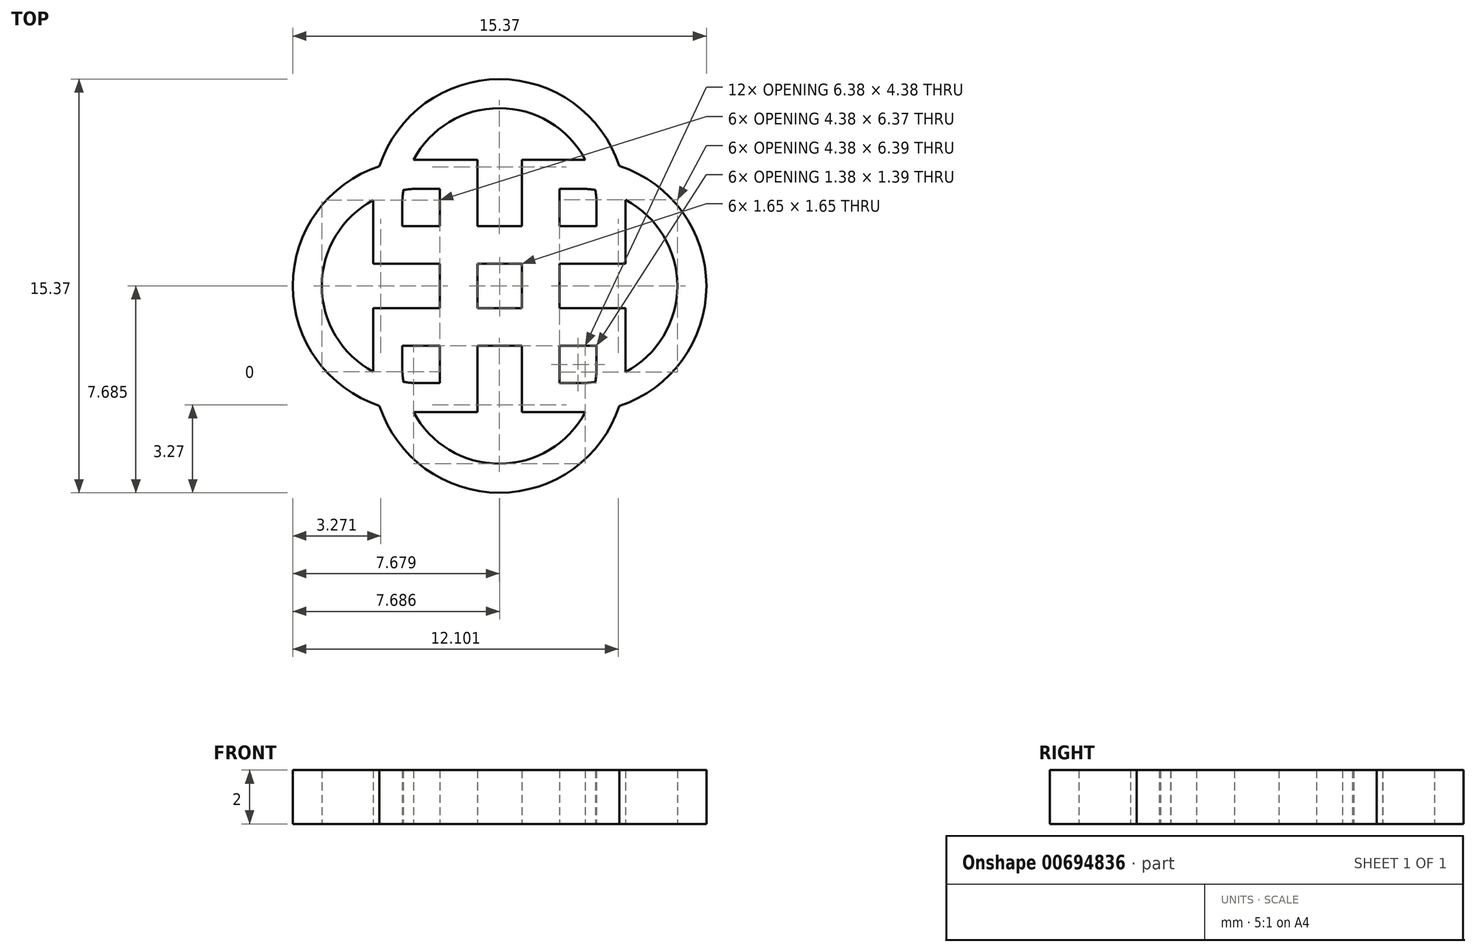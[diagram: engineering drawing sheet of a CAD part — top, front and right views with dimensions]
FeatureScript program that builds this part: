
annotation { "Feature Type Name" : "Feature", "Feature Type Description" : "" }
export const myFeature = defineFeature(function(context is Context, id is Id, definition is map)
    precondition{}
    {
        {
            var Q0;
            Q0=qCreatedBy(makeId("Top.planeOp"),FACE);
            var sketch = newSketch(context, id + "F0", { "sketchPlane" : qUnion([Q0])});
            skPoint(sketch, "E0", {"position": v(-20.72, -15.85) * mm});
            skPoint(sketch, "E1", {"position": v(-17.72, -15.85) * mm});
            skArc(sketch, "E2", {"start": v(-20.72, -11.16) * mm, "mid": v(-25.4, -15.85) * mm, "end": v(-20.72, -20.53) * mm});
            skArc(sketch, "E3", {"start": v(-20.72, -12.24) * mm, "mid": v(-24.33, -15.85) * mm, "end": v(-20.72, -19.46) * mm});
            skLineSegment(sketch, "E4", {"start": v(-20.72, -10.41) * mm, "end": v(-20.72, -21) * mm, "construction": true});
            skLineSegment(sketch, "E5", {"start": v(-20.72, -11.16) * mm, "end": v(-18.55, -11.16) * mm});
            skLineSegment(sketch, "E6", {"start": v(-18.55, -11.16) * mm, "end": v(-18.55, -20.53) * mm});
            skLineSegment(sketch, "E7", {"start": v(-18.55, -20.53) * mm, "end": v(-20.72, -20.53) * mm});
            skLineSegment(sketch, "E8", {"start": v(-20.72, -12.24) * mm, "end": v(-19.95, -12.24) * mm});
            skLineSegment(sketch, "E9", {"start": v(-19.95, -12.24) * mm, "end": v(-19.95, -19.46) * mm});
            skLineSegment(sketch, "E10", {"start": v(-19.95, -19.46) * mm, "end": v(-20.72, -19.46) * mm});
            skPoint(sketch, "E11", {"position": v(-17.73, -12.85) * mm});
            skPoint(sketch, "E12", {"position": v(-17.73, -15.85) * mm});
            skArc(sketch, "E13", {"start": v(-13.04, -12.85) * mm, "mid": v(-17.73, -8.16) * mm, "end": v(-22.42, -12.85) * mm});
            skArc(sketch, "E14", {"start": v(-14.12, -12.85) * mm, "mid": v(-17.73, -9.24) * mm, "end": v(-21.34, -12.85) * mm});
            skLineSegment(sketch, "E15", {"start": v(-13.04, -12.85) * mm, "end": v(-13.04, -15.02) * mm});
            skLineSegment(sketch, "E16", {"start": v(-13.04, -15.02) * mm, "end": v(-22.42, -15.02) * mm});
            skLineSegment(sketch, "E17", {"start": v(-22.42, -15.02) * mm, "end": v(-22.42, -12.85) * mm});
            skLineSegment(sketch, "E18", {"start": v(-14.12, -12.85) * mm, "end": v(-14.12, -13.62) * mm});
            skLineSegment(sketch, "E19", {"start": v(-14.12, -13.62) * mm, "end": v(-21.34, -13.62) * mm});
            skLineSegment(sketch, "E20", {"start": v(-21.34, -13.62) * mm, "end": v(-21.34, -12.85) * mm});
            skLineSegment(sketch, "E21.MirrorCS", {"start": v(-16.9, -11.16) * mm, "end": v(-16.9, -20.53) * mm});
            skLineSegment(sketch, "E22.MirrorCS", {"start": v(-16.9, -20.53) * mm, "end": v(-14.73, -20.53) * mm});
            skArc(sketch, "E23.MirrorCS", {"start": v(-14.73, -11.16) * mm, "mid": v(-10.04, -15.85) * mm, "end": v(-14.73, -20.53) * mm});
            skLineSegment(sketch, "E24.MirrorCS", {"start": v(-15.5, -19.46) * mm, "end": v(-14.73, -19.46) * mm});
            skArc(sketch, "E25.MirrorCS", {"start": v(-14.73, -12.24) * mm, "mid": v(-11.12, -15.85) * mm, "end": v(-14.73, -19.46) * mm});
            skLineSegment(sketch, "E26.MirrorCS", {"start": v(-15.5, -12.24) * mm, "end": v(-15.5, -19.46) * mm});
            skLineSegment(sketch, "E27.MirrorCS", {"start": v(-14.73, -12.24) * mm, "end": v(-15.5, -12.24) * mm});
            skLineSegment(sketch, "E28.MirrorCS", {"start": v(-14.73, -11.16) * mm, "end": v(-16.9, -11.16) * mm});
            skLineSegment(sketch, "E29.MirrorCS", {"start": v(-13.04, -16.67) * mm, "end": v(-22.42, -16.67) * mm});
            skLineSegment(sketch, "E30.MirrorCS", {"start": v(-14.12, -18.07) * mm, "end": v(-21.34, -18.07) * mm});
            skLineSegment(sketch, "E31.MirrorCS", {"start": v(-22.42, -16.67) * mm, "end": v(-22.42, -18.84) * mm});
            skArc(sketch, "E32.MirrorCS", {"start": v(-13.04, -18.84) * mm, "mid": v(-17.73, -23.53) * mm, "end": v(-22.42, -18.84) * mm});
            skArc(sketch, "E33.MirrorCS", {"start": v(-14.12, -18.84) * mm, "mid": v(-17.73, -22.45) * mm, "end": v(-21.34, -18.84) * mm});
            skLineSegment(sketch, "E34.MirrorCS", {"start": v(-21.34, -18.07) * mm, "end": v(-21.34, -18.84) * mm});
            skLineSegment(sketch, "E35.MirrorCS", {"start": v(-14.12, -18.84) * mm, "end": v(-14.12, -18.07) * mm});
            skLineSegment(sketch, "E36.MirrorCS", {"start": v(-13.04, -18.84) * mm, "end": v(-13.04, -16.67) * mm});
            skSolve(sketch);
        }
        {
            var Q0;
            Q0 = qSketchRegion(id + "F0", true);
            var Q1;
            {var subQ4=sQuery(id+"F0.wireOp",EDGE,"E17");Q1=makeQuery(id+"F0.imprint","IMPRINT",FACE,{"disambiguationData":[TD([[makeQuery(id+"F0.imprint","IMPRINT",EDGE,{"derivedFrom":subQ4}),-1.0]])]});}
            var Q2;
            {var subQ0=sQuery(id+"F0.wireOp",EDGE,"E19");var subQ1=sQuery(id+"F0.wireOp",EDGE,"E6");var subQ2=makeQuery(id+"F0.imprint","INTERSECT",VERTEX,{"derivedFrom":[subQ1,subQ0]});Q2=makeQuery(id+"F0.imprint","IMPRINT",FACE,{"disambiguationData":[TD([[makeQuery(id+"F0.imprint","IMPRINT",EDGE,{"disambiguationData":[TD([[subQ2,-1.0]])],"derivedFrom":subQ1}),-1.0]])]});}
            var Q3;
            {var subQ1=sQuery(id+"F0.wireOp",EDGE,"E5");Q3=makeQuery(id+"F0.imprint","IMPRINT",FACE,{"disambiguationData":[TD([[makeQuery(id+"F0.imprint","IMPRINT",EDGE,{"derivedFrom":subQ1}),-1.0]])]});}
            var Q4;
            {var subQ0=sQuery(id+"F0.wireOp",EDGE,"E19");var subQ1=sQuery(id+"F0.wireOp",EDGE,"E6");var subQ2=makeQuery(id+"F0.imprint","INTERSECT",VERTEX,{"derivedFrom":[subQ1,subQ0]});Q4=makeQuery(id+"F0.imprint","IMPRINT",FACE,{"disambiguationData":[TD([[makeQuery(id+"F0.imprint","IMPRINT",EDGE,{"disambiguationData":[TD([[subQ2,-1.0]])],"derivedFrom":subQ1}),1.0]])]});}
            var Q5;
            {var subQ0=sQuery(id+"F0.wireOp",EDGE,"E26.MirrorCS");var subQ1=sQuery(id+"F0.wireOp",EDGE,"E16");var subQ2=makeQuery(id+"F0.imprint","INTERSECT",VERTEX,{"derivedFrom":[subQ1,subQ0]});Q5=makeQuery(id+"F0.imprint","IMPRINT",FACE,{"disambiguationData":[TD([[makeQuery(id+"F0.imprint","IMPRINT",EDGE,{"disambiguationData":[TD([[subQ2,-1.0]])],"derivedFrom":subQ1}),-1.0]])]});}
            var Q6;
            {var subQ1=sQuery(id+"F0.wireOp",EDGE,"E15");Q6=makeQuery(id+"F0.imprint","IMPRINT",FACE,{"disambiguationData":[TD([[makeQuery(id+"F0.imprint","IMPRINT",EDGE,{"derivedFrom":subQ1}),-1.0]])]});}
            var Q7;
            {var subQ9=sQuery(id+"F0.wireOp",EDGE,"E27.MirrorCS");Q7=makeQuery(id+"F0.imprint","IMPRINT",FACE,{"disambiguationData":[TD([[makeQuery(id+"F0.imprint","IMPRINT",EDGE,{"derivedFrom":subQ9}),-1.0]])]});}
            var Q8;
            {var subQ2=sQuery(id+"F0.wireOp",EDGE,"E22.MirrorCS");Q8=makeQuery(id+"F0.imprint","IMPRINT",FACE,{"disambiguationData":[TD([[makeQuery(id+"F0.imprint","IMPRINT",EDGE,{"derivedFrom":subQ2}),1.0]])]});}
            var Q9;
            {var subQ4=sQuery(id+"F0.wireOp",EDGE,"E35.MirrorCS");Q9=makeQuery(id+"F0.imprint","IMPRINT",FACE,{"disambiguationData":[TD([[makeQuery(id+"F0.imprint","IMPRINT",EDGE,{"derivedFrom":subQ4}),-1.0]])]});}
            var Q10;
            {var subQ0=sQuery(id+"F0.wireOp",EDGE,"E29.MirrorCS");var subQ1=sQuery(id+"F0.wireOp",EDGE,"E21.MirrorCS");var subQ2=makeQuery(id+"F0.imprint","INTERSECT",VERTEX,{"derivedFrom":[subQ1,subQ0]});Q10=makeQuery(id+"F0.imprint","IMPRINT",FACE,{"disambiguationData":[TD([[makeQuery(id+"F0.imprint","IMPRINT",EDGE,{"disambiguationData":[TD([[subQ2,-1.0]])],"derivedFrom":subQ1}),1.0]])]});}
            var Q11;
            {var subQ0=sQuery(id+"F0.wireOp",EDGE,"E26.MirrorCS");var subQ1=sQuery(id+"F0.wireOp",EDGE,"E16");var subQ2=makeQuery(id+"F0.imprint","INTERSECT",VERTEX,{"derivedFrom":[subQ1,subQ0]});Q11=makeQuery(id+"F0.imprint","IMPRINT",FACE,{"disambiguationData":[TD([[makeQuery(id+"F0.imprint","IMPRINT",EDGE,{"disambiguationData":[TD([[subQ2,-1.0]])],"derivedFrom":subQ1}),1.0]])]});}
            var Q12;
            {var subQ0=sQuery(id+"F0.wireOp",EDGE,"E29.MirrorCS");var subQ1=sQuery(id+"F0.wireOp",EDGE,"E6");var subQ2=makeQuery(id+"F0.imprint","INTERSECT",VERTEX,{"derivedFrom":[subQ1,subQ0]});Q12=makeQuery(id+"F0.imprint","IMPRINT",FACE,{"disambiguationData":[TD([[makeQuery(id+"F0.imprint","IMPRINT",EDGE,{"disambiguationData":[TD([[subQ2,-1.0]])],"derivedFrom":subQ1}),-1.0]])]});}
            var Q13;
            {var subQ0=sQuery(id+"F0.wireOp",EDGE,"E16");var subQ1=sQuery(id+"F0.wireOp",EDGE,"E6");var subQ2=makeQuery(id+"F0.imprint","INTERSECT",VERTEX,{"derivedFrom":[subQ1,subQ0]});Q13=makeQuery(id+"F0.imprint","IMPRINT",FACE,{"disambiguationData":[TD([[makeQuery(id+"F0.imprint","IMPRINT",EDGE,{"disambiguationData":[TD([[subQ2,-1.0]])],"derivedFrom":subQ1}),-1.0]])]});}
            var Q14;
            {var subQ0=sQuery(id+"F0.wireOp",EDGE,"E29.MirrorCS");var subQ1=sQuery(id+"F0.wireOp",EDGE,"E6");var subQ2=makeQuery(id+"F0.imprint","INTERSECT",VERTEX,{"derivedFrom":[subQ1,subQ0]});Q14=makeQuery(id+"F0.imprint","IMPRINT",FACE,{"disambiguationData":[TD([[makeQuery(id+"F0.imprint","IMPRINT",EDGE,{"disambiguationData":[TD([[subQ2,-1.0]])],"derivedFrom":subQ1}),1.0]])]});}
            var Q15;
            {var subQ0=sQuery(id+"F0.wireOp",EDGE,"E7");Q15=makeQuery(id+"F0.imprint","IMPRINT",FACE,{"disambiguationData":[TD([[makeQuery(id+"F0.imprint","IMPRINT",EDGE,{"derivedFrom":subQ0}),-1.0]])]});}
            var Q16;
            {var subQ0=sQuery(id+"F0.wireOp",EDGE,"E31.MirrorCS");Q16=makeQuery(id+"F0.imprint","IMPRINT",FACE,{"disambiguationData":[TD([[makeQuery(id+"F0.imprint","IMPRINT",EDGE,{"derivedFrom":subQ0}),1.0]])]});}
            extrude(context, id + "F1", {"entities" : qUnion([Q0, Q1, Q2, Q3, Q4, Q5, Q6, Q7, Q8, Q9, Q10, Q11, Q12, Q13, Q14, Q15, Q16]), "depth" : 2 * mm, "offsetDistance" : 25 * mm});
        }
    });
